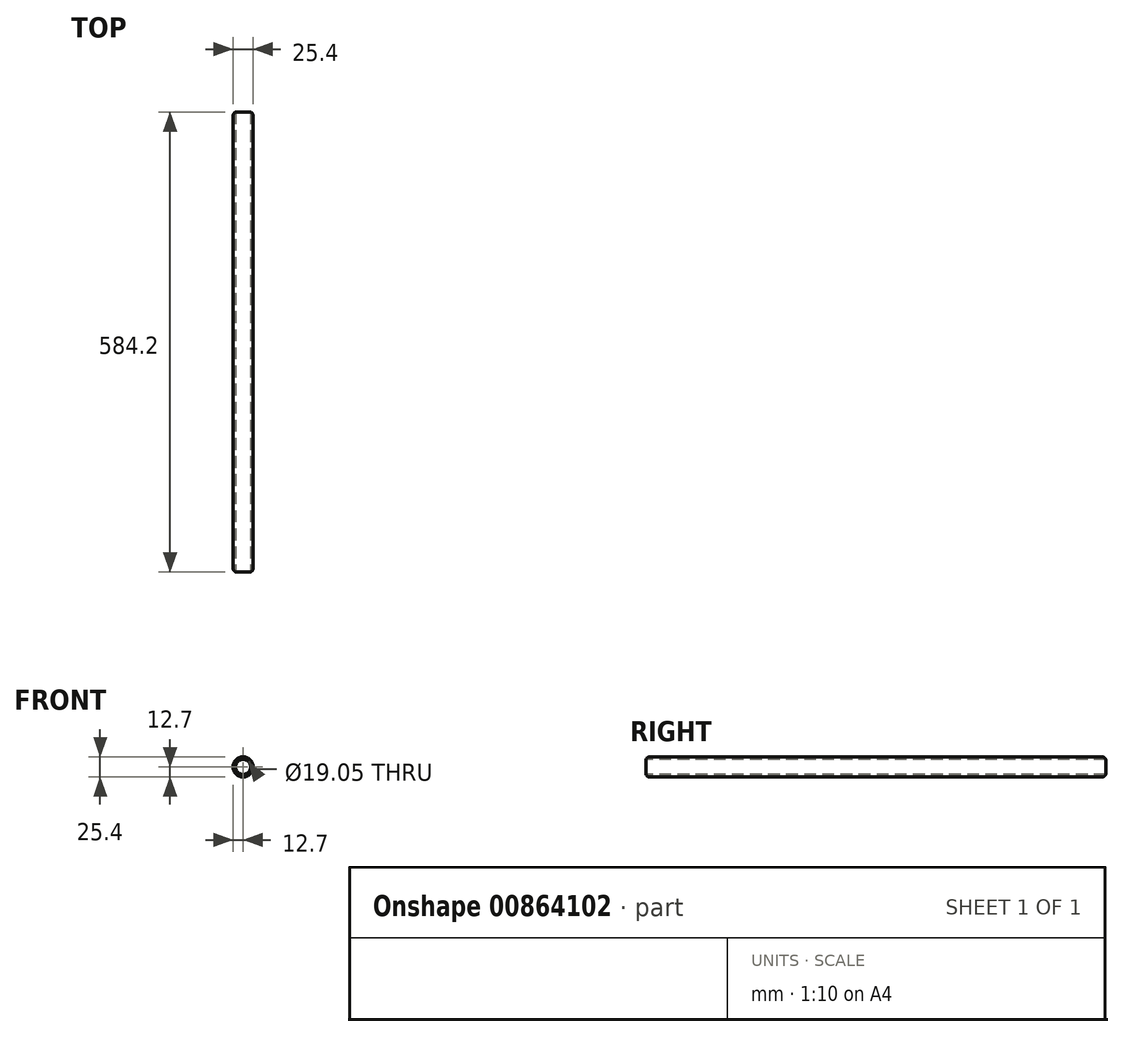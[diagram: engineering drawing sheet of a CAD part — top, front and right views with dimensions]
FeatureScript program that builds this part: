
annotation { "Feature Type Name" : "Feature", "Feature Type Description" : "" }
export const myFeature = defineFeature(function(context is Context, id is Id, definition is map)
    precondition{}
    {
        {
            var Q0;
            Q0=qCreatedBy(makeId("Front.planeOp"),FACE);
            var sketch = newSketch(context, id + "F0", { "sketchPlane" : qUnion([Q0])});
            skCircle(sketch, "E0", {"center": v(0, 0) * mm, "radius": 12.7 * mm});
            skSolve(sketch);
        }
        {
            var Q0;
            Q0=makeQuery(id+"F0.imprint","IMPRINT",FACE,{"disambiguationData":[TD([[makeQuery(id+"F0.imprint","IMPRINT",EDGE,{"derivedFrom":sQuery(id+"F0.wireOp",EDGE,"E0")}),1.0]])]});
            extrude(context, id + "F1", {"entities" : qUnion([Q0]), "depth" : 584.2 * mm, "offsetDistance" : 25.4 * mm});
        }
        {
            var Q0;
            Q0=makeQuery(id+"F1.opExtrude","CAP_FACE",FACE,{"disambiguationData":[OSD([sQuery(id+"F0.wireOp",EDGE,"E0")])],"isStart":false});
            var sketch = newSketch(context, id + "F2", { "sketchPlane" : qUnion([Q0])});
            skCircle(sketch, "E1", {"center": v(0, 0) * mm, "radius": 9.53 * mm});
            skSolve(sketch);
        }
        {
            var Q0;
            Q0=makeQuery(id+"F2.imprint","IMPRINT",FACE,{"disambiguationData":[TD([[makeQuery(id+"F2.imprint","IMPRINT",EDGE,{"derivedFrom":sQuery(id+"F2.wireOp",EDGE,"E1")}),1.0]])]});
            extrude(context, id + "F3", {"entities" : qUnion([Q0]), "operationType" : NewBodyOperationType.REMOVE, "endBound" : BoundingType.THROUGH_ALL, "oppositeDirection" : true, "depth" : 25.4 * mm, "offsetDistance" : 25.4 * mm});
        }
        {
            var Q0;
            Q0=makeQuery(id+"F1.opExtrude","CAP_EDGE",EDGE,{"disambiguationData":[OSD([sQuery(id+"F0.wireOp",EDGE,"E0")])],"isStart":false});
            var Q1;
            Q1=makeQuery(id+"F1.opExtrude","CAP_EDGE",EDGE,{"disambiguationData":[OSD([sQuery(id+"F0.wireOp",EDGE,"E0")])],"isStart":true});
            fillet(context, id + "F4", {"entities" : qUnion([Q0, Q1]), "radius" : 5.08 * mm, "tangentPropagation" : true, "allowEdgeOverflow" : false});
        }
    });
